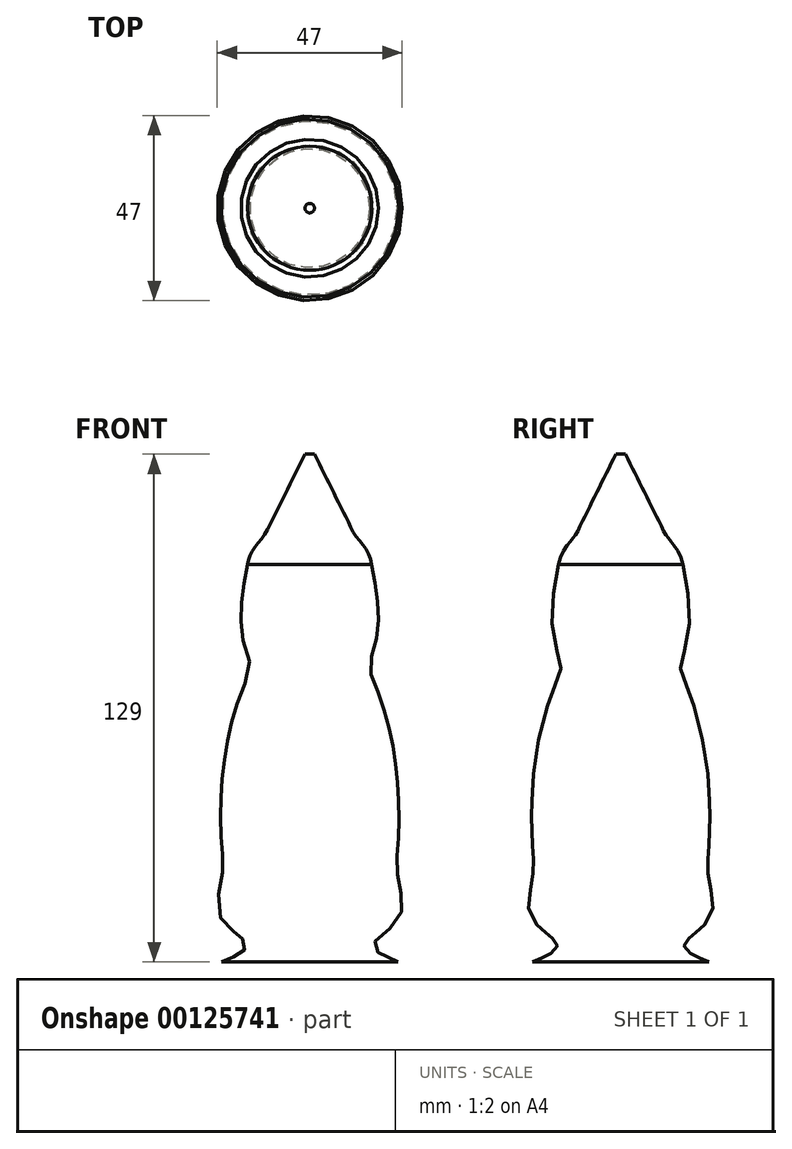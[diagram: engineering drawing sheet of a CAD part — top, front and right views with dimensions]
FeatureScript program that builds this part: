
annotation { "Feature Type Name" : "Feature", "Feature Type Description" : "" }
export const myFeature = defineFeature(function(context is Context, id is Id, definition is map)
    precondition{}
    {
        {
            var Q0;
            Q0=qCreatedBy(makeId("Top.planeOp"),FACE);
            cPlane(context, id + "F0", {"entities" : qUnion([Q0]), "cplaneType" : CPlaneType.OFFSET, "offset" : 41 * mm, "oppositeDirection" : true, "width" : 150 * mm, "height" : 150 * mm});
        }
        {
            var Q0;
            Q0=qCreatedBy(id+"F0.planeOp",FACE);
            var sketch = newSketch(context, id + "F1", { "sketchPlane" : qUnion([Q0])});
            skCircle(sketch, "E0", {"center": v(0, 0) * mm, "radius": 22.6 * mm});
            skSolve(sketch);
        }
        {
            var Q0;
            Q0=qCreatedBy(id+"F0.planeOp",FACE);
            cPlane(context, id + "F2", {"entities" : qUnion([Q0]), "cplaneType" : CPlaneType.OFFSET, "offset" : 60 * mm, "width" : 150 * mm, "height" : 150 * mm});
        }
        {
            var Q0;
            Q0=qCreatedBy(id+"F2.planeOp",FACE);
            var sketch = newSketch(context, id + "F3", { "sketchPlane" : qUnion([Q0])});
            skCircle(sketch, "E1", {"center": v(0, 0) * mm, "radius": 16.36 * mm});
            skSolve(sketch);
        }
        {
            var Q0;
            Q0=qCreatedBy(id+"F0.planeOp",FACE);
            cPlane(context, id + "F4", {"entities" : qUnion([Q0]), "cplaneType" : CPlaneType.OFFSET, "offset" : 7 * mm, "oppositeDirection" : true, "width" : 150 * mm, "height" : 150 * mm});
        }
        {
            var Q0;
            Q0=qCreatedBy(id+"F4.planeOp",FACE);
            var sketch = newSketch(context, id + "F5", { "sketchPlane" : qUnion([Q0])});
            skCircle(sketch, "E2", {"center": v(0, 0) * mm, "radius": 16.12 * mm});
            skSolve(sketch);
        }
        {
            var Q0;
            Q0=qCreatedBy(id+"F4.planeOp",FACE);
            cPlane(context, id + "F6", {"entities" : qUnion([Q0]), "cplaneType" : CPlaneType.OFFSET, "offset" : 4 * mm, "oppositeDirection" : true, "width" : 150 * mm, "height" : 150 * mm});
        }
        {
            var Q0;
            Q0=qCreatedBy(id+"F6.planeOp",FACE);
            var sketch = newSketch(context, id + "F7", { "sketchPlane" : qUnion([Q0])});
            skCircle(sketch, "E3", {"center": v(0, 0) * mm, "radius": 22.39 * mm});
            skSolve(sketch);
        }
        {
            var Q0;
            Q0=qCreatedBy(id+"F2.planeOp",FACE);
            cPlane(context, id + "F8", {"entities" : qUnion([Q0]), "cplaneType" : CPlaneType.OFFSET, "offset" : 30 * mm, "oppositeDirection" : true, "width" : 150 * mm, "height" : 150 * mm});
        }
        {
            var Q0;
            Q0=qCreatedBy(id+"F8.planeOp",FACE);
            var sketch = newSketch(context, id + "F9", { "sketchPlane" : qUnion([Q0])});
            skCircle(sketch, "E4", {"center": v(0, 0) * mm, "radius": 22.55 * mm});
            skSolve(sketch);
        }
        {
            var Q0;
            Q0=qCreatedBy(id+"F8.planeOp",FACE);
            cPlane(context, id + "F10", {"entities" : qUnion([Q0]), "cplaneType" : CPlaneType.OFFSET, "offset" : 10 * mm, "oppositeDirection" : true, "width" : 150 * mm, "height" : 150 * mm});
        }
        {
            var Q0;
            Q0=qCreatedBy(id+"F10.planeOp",FACE);
            var sketch = newSketch(context, id + "F11", { "sketchPlane" : qUnion([Q0])});
            skCircle(sketch, "E5", {"center": v(0, 0) * mm, "radius": 22.46 * mm});
            skSolve(sketch);
        }
        {
            var Q0;
            Q0=qCreatedBy(id+"F10.planeOp",FACE);
            cPlane(context, id + "F12", {"entities" : qUnion([Q0]), "cplaneType" : CPlaneType.OFFSET, "offset" : 10 * mm, "oppositeDirection" : true, "width" : 150 * mm, "height" : 150 * mm});
        }
        {
            var Q0;
            Q0=qCreatedBy(id+"F12.planeOp",FACE);
            var sketch = newSketch(context, id + "F13", { "sketchPlane" : qUnion([Q0])});
            skCircle(sketch, "E6", {"center": v(0, 0) * mm, "radius": 22.4 * mm});
            skSolve(sketch);
        }
        {
            var Q0;
            Q0=qCreatedBy(id+"F2.planeOp",FACE);
            cPlane(context, id + "F14", {"entities" : qUnion([Q0]), "cplaneType" : CPlaneType.OFFSET, "offset" : 4 * mm, "width" : 150 * mm, "height" : 150 * mm});
        }
        {
            var Q0;
            Q0=qCreatedBy(id+"F14.planeOp",FACE);
            var sketch = newSketch(context, id + "F15", { "sketchPlane" : qUnion([Q0])});
            skCircle(sketch, "E7", {"center": v(0, 0) * mm, "radius": 15.17 * mm});
            skSolve(sketch);
        }
        {
            var Q0;
            Q0=qCreatedBy(id+"F14.planeOp",FACE);
            cPlane(context, id + "F16", {"entities" : qUnion([Q0]), "cplaneType" : CPlaneType.OFFSET, "offset" : 4 * mm, "width" : 150 * mm, "height" : 150 * mm});
        }
        {
            var Q0;
            Q0=qCreatedBy(id+"F16.planeOp",FACE);
            var sketch = newSketch(context, id + "F17", { "sketchPlane" : qUnion([Q0])});
            skCircle(sketch, "E8", {"center": v(0, 0) * mm, "radius": 16.2 * mm});
            skSolve(sketch);
        }
        {
            var Q0;
            Q0=qCreatedBy(id+"F16.planeOp",FACE);
            cPlane(context, id + "F18", {"entities" : qUnion([Q0]), "cplaneType" : CPlaneType.OFFSET, "offset" : 22 * mm, "width" : 150 * mm, "height" : 150 * mm});
        }
        {
            var Q0;
            Q0=qCreatedBy(id+"F18.planeOp",FACE);
            var sketch = newSketch(context, id + "F19", { "sketchPlane" : qUnion([Q0])});
            skCircle(sketch, "E9", {"center": v(0, 0) * mm, "radius": 15.76 * mm});
            skSolve(sketch);
        }
        {
            var Q0;
            Q0=qCreatedBy(id+"F18.planeOp",FACE);
            cPlane(context, id + "F20", {"entities" : qUnion([Q0]), "cplaneType" : CPlaneType.OFFSET, "offset" : 2 * mm, "width" : 150 * mm, "height" : 150 * mm});
        }
        {
            var Q0;
            Q0=qCreatedBy(id+"F20.planeOp",FACE);
            var sketch = newSketch(context, id + "F21", { "sketchPlane" : qUnion([Q0])});
            skCircle(sketch, "E10", {"center": v(0, 0) * mm, "radius": 15.2 * mm});
            skSolve(sketch);
        }
        {
            var Q0;
            Q0=qCreatedBy(id+"F20.planeOp",FACE);
            cPlane(context, id + "F22", {"entities" : qUnion([Q0]), "cplaneType" : CPlaneType.OFFSET, "offset" : 2 * mm, "width" : 150 * mm, "height" : 150 * mm});
        }
        {
            var Q0;
            Q0=qCreatedBy(id+"F22.planeOp",FACE);
            var sketch = newSketch(context, id + "F23", { "sketchPlane" : qUnion([Q0])});
            skCircle(sketch, "E11", {"center": v(0, 0) * mm, "radius": 14.2 * mm});
            skSolve(sketch);
        }
        {
            var Q0;
            Q0=qCreatedBy(id+"F22.planeOp",FACE);
            cPlane(context, id + "F24", {"entities" : qUnion([Q0]), "cplaneType" : CPlaneType.OFFSET, "offset" : 2 * mm, "width" : 150 * mm, "height" : 150 * mm});
        }
        {
            var Q0;
            Q0=qCreatedBy(id+"F24.planeOp",FACE);
            cPlane(context, id + "F25", {"entities" : qUnion([Q0]), "cplaneType" : CPlaneType.OFFSET, "offset" : 2 * mm, "width" : 150 * mm, "height" : 150 * mm});
        }
        {
            var Q0;
            Q0=qCreatedBy(id+"F25.planeOp",FACE);
            var sketch = newSketch(context, id + "F26", { "sketchPlane" : qUnion([Q0])});
            skCircle(sketch, "E12", {"center": v(0, 0) * mm, "radius": 11.2 * mm});
            skSolve(sketch);
        }
        {
            var Q0;
            Q0=qCreatedBy(id+"F25.planeOp",FACE);
            cPlane(context, id + "F27", {"entities" : qUnion([Q0]), "cplaneType" : CPlaneType.OFFSET, "offset" : 2 * mm, "width" : 150 * mm, "height" : 150 * mm});
        }
        {
            var Q0;
            Q0=qCreatedBy(id+"F27.planeOp",FACE);
            var sketch = newSketch(context, id + "F28", { "sketchPlane" : qUnion([Q0])});
            skCircle(sketch, "E13", {"center": v(0, 0) * mm, "radius": 10.2 * mm});
            skSolve(sketch);
        }
        {
            var Q0;
            Q0=qCreatedBy(id+"F27.planeOp",FACE);
            cPlane(context, id + "F29", {"entities" : qUnion([Q0]), "cplaneType" : CPlaneType.OFFSET, "offset" : 2 * mm, "width" : 150 * mm, "height" : 150 * mm});
        }
        {
            var Q0;
            Q0=qCreatedBy(id+"F29.planeOp",FACE);
            var sketch = newSketch(context, id + "F30", { "sketchPlane" : qUnion([Q0])});
            skCircle(sketch, "E14", {"center": v(0, 0) * mm, "radius": 9.2 * mm});
            skSolve(sketch);
        }
        {
            var Q0;
            Q0=qCreatedBy(id+"F29.planeOp",FACE);
            cPlane(context, id + "F31", {"entities" : qUnion([Q0]), "cplaneType" : CPlaneType.OFFSET, "offset" : 2 * mm, "width" : 150 * mm, "height" : 150 * mm});
        }
        {
            var Q0;
            Q0=qCreatedBy(id+"F31.planeOp",FACE);
            var sketch = newSketch(context, id + "F32", { "sketchPlane" : qUnion([Q0])});
            skCircle(sketch, "E15", {"center": v(0, 0) * mm, "radius": 8.2 * mm});
            skSolve(sketch);
        }
        {
            var Q0;
            Q0=qCreatedBy(id+"F31.planeOp",FACE);
            cPlane(context, id + "F33", {"entities" : qUnion([Q0]), "cplaneType" : CPlaneType.OFFSET, "offset" : 2 * mm, "width" : 150 * mm, "height" : 150 * mm});
        }
        {
            var Q0;
            Q0=qCreatedBy(id+"F33.planeOp",FACE);
            var sketch = newSketch(context, id + "F34", { "sketchPlane" : qUnion([Q0])});
            skCircle(sketch, "E16", {"center": v(0, 0) * mm, "radius": 7.2 * mm});
            skSolve(sketch);
        }
        {
            var Q0;
            Q0=qCreatedBy(id+"F33.planeOp",FACE);
            cPlane(context, id + "F35", {"entities" : qUnion([Q0]), "cplaneType" : CPlaneType.OFFSET, "offset" : 2 * mm, "width" : 150 * mm, "height" : 150 * mm});
        }
        {
            var Q0;
            Q0=qCreatedBy(id+"F35.planeOp",FACE);
            var sketch = newSketch(context, id + "F36", { "sketchPlane" : qUnion([Q0])});
            skCircle(sketch, "E17", {"center": v(0, 0) * mm, "radius": 6.2 * mm});
            skSolve(sketch);
        }
        {
            var Q0;
            Q0=qCreatedBy(id+"F35.planeOp",FACE);
            cPlane(context, id + "F37", {"entities" : qUnion([Q0]), "cplaneType" : CPlaneType.OFFSET, "offset" : 2 * mm, "width" : 150 * mm, "height" : 150 * mm});
        }
        {
            var Q0;
            Q0=qCreatedBy(id+"F37.planeOp",FACE);
            var sketch = newSketch(context, id + "F38", { "sketchPlane" : qUnion([Q0])});
            skCircle(sketch, "E18", {"center": v(0, 0) * mm, "radius": 5.2 * mm});
            skSolve(sketch);
        }
        {
            var Q0;
            Q0=qCreatedBy(id+"F37.planeOp",FACE);
            cPlane(context, id + "F39", {"entities" : qUnion([Q0]), "cplaneType" : CPlaneType.OFFSET, "offset" : 2 * mm, "width" : 150 * mm, "height" : 150 * mm});
        }
        {
            var Q0;
            Q0=qCreatedBy(id+"F39.planeOp",FACE);
            var sketch = newSketch(context, id + "F40", { "sketchPlane" : qUnion([Q0])});
            skCircle(sketch, "E19", {"center": v(0, 0) * mm, "radius": 4.2 * mm});
            skSolve(sketch);
        }
        {
            var Q0;
            Q0=qCreatedBy(id+"F39.planeOp",FACE);
            cPlane(context, id + "F41", {"entities" : qUnion([Q0]), "cplaneType" : CPlaneType.OFFSET, "offset" : 2 * mm, "width" : 150 * mm, "height" : 150 * mm});
        }
        {
            var Q0;
            Q0=qCreatedBy(id+"F41.planeOp",FACE);
            var sketch = newSketch(context, id + "F42", { "sketchPlane" : qUnion([Q0])});
            skCircle(sketch, "E20", {"center": v(0, 0) * mm, "radius": 3.2 * mm});
            skSolve(sketch);
        }
        {
            var Q0;
            Q0=qCreatedBy(id+"F41.planeOp",FACE);
            cPlane(context, id + "F43", {"entities" : qUnion([Q0]), "cplaneType" : CPlaneType.OFFSET, "offset" : 2 * mm, "width" : 150 * mm, "height" : 150 * mm});
        }
        {
            var Q0;
            Q0=qCreatedBy(id+"F43.planeOp",FACE);
            var sketch = newSketch(context, id + "F44", { "sketchPlane" : qUnion([Q0])});
            skCircle(sketch, "E21", {"center": v(0, 0) * mm, "radius": 2.2 * mm});
            skSolve(sketch);
        }
        {
            var Q0;
            Q0=qCreatedBy(id+"F43.planeOp",FACE);
            cPlane(context, id + "F45", {"entities" : qUnion([Q0]), "cplaneType" : CPlaneType.OFFSET, "offset" : 2 * mm, "width" : 150 * mm, "height" : 150 * mm});
        }
        {
            var Q0;
            Q0=qCreatedBy(id+"F45.planeOp",FACE);
            var sketch = newSketch(context, id + "F46", { "sketchPlane" : qUnion([Q0])});
            skCircle(sketch, "E22", {"center": v(0, 0) * mm, "radius": 1.2 * mm});
            skSolve(sketch);
        }
        {
            var Q0;
            Q0 = qSketchRegion(id + "F46", true);
            var Q1;
            Q1 = qSketchRegion(id + "F44", true);
            var Q2;
            Q2 = qSketchRegion(id + "F42", true);
            var Q3;
            Q3 = qSketchRegion(id + "F40", true);
            var Q4;
            Q4 = qSketchRegion(id + "F38", true);
            var Q5;
            Q5 = qSketchRegion(id + "F36", true);
            var Q6;
            Q6 = qSketchRegion(id + "F34", true);
            var Q7;
            Q7 = qSketchRegion(id + "F32", true);
            var Q8;
            Q8 = qSketchRegion(id + "F30", true);
            var Q9;
            Q9 = qSketchRegion(id + "F28", true);
            var Q10;
            Q10 = qSketchRegion(id + "F26", true);
            var Q11;
            Q11 = qSketchRegion(id + "F23", true);
            var Q12;
            Q12 = qSketchRegion(id + "F21", true);
            var Q13;
            Q13 = qSketchRegion(id + "F19", true);
            loft(context, id + "F47", {"sheetProfilesArray" : [{ "sheetProfileEntities" : qUnion([Q0]) }, { "sheetProfileEntities" : qUnion([Q1]) }, { "sheetProfileEntities" : qUnion([Q2]) }, { "sheetProfileEntities" : qUnion([Q3]) }, { "sheetProfileEntities" : qUnion([Q4]) }, { "sheetProfileEntities" : qUnion([Q5]) }, { "sheetProfileEntities" : qUnion([Q6]) }, { "sheetProfileEntities" : qUnion([Q7]) }, { "sheetProfileEntities" : qUnion([Q8]) }, { "sheetProfileEntities" : qUnion([Q9]) }, { "sheetProfileEntities" : qUnion([Q10]) }, { "sheetProfileEntities" : qUnion([Q11]) }, { "sheetProfileEntities" : qUnion([Q12]) }, { "sheetProfileEntities" : qUnion([Q13]) }]});
        }
        {
            var Q0;
            Q0 = qSketchRegion(id + "F19", true);
            var Q1;
            Q1 = qSketchRegion(id + "F17", true);
            var Q2;
            Q2 = qSketchRegion(id + "F15", true);
            var Q3;
            Q3 = qSketchRegion(id + "F3", true);
            var Q4;
            Q4 = qSketchRegion(id + "F9", true);
            var Q5;
            Q5 = qSketchRegion(id + "F11", true);
            var Q6;
            Q6 = qSketchRegion(id + "F13", true);
            var Q7;
            Q7 = qSketchRegion(id + "F1", true);
            var Q8;
            Q8 = qSketchRegion(id + "F5", true);
            var Q9;
            Q9 = qSketchRegion(id + "F7", true);
            loft(context, id + "F48", {"sheetProfilesArray" : [{ "sheetProfileEntities" : qUnion([Q0]) }, { "sheetProfileEntities" : qUnion([Q1]) }, { "sheetProfileEntities" : qUnion([Q2]) }, { "sheetProfileEntities" : qUnion([Q3]) }, { "sheetProfileEntities" : qUnion([Q4]) }, { "sheetProfileEntities" : qUnion([Q5]) }, { "sheetProfileEntities" : qUnion([Q6]) }, { "sheetProfileEntities" : qUnion([Q7]) }, { "sheetProfileEntities" : qUnion([Q8]) }, { "sheetProfileEntities" : qUnion([Q9]) }]});
        }
    });
